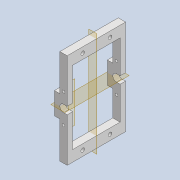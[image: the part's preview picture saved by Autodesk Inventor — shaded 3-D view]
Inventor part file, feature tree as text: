
AUTODESK INVENTOR PART (.ipt)
format: ipt  version: 2020 (Build 240168000, 168)  size: 174,080 bytes
history: native  units: mm
features: reference x8, other x6, extrude x4, sketch x4, plane x3, mirror x2, projected_geometry x2
ambient origin geometry x8: Origin, YZ Plane, XZ Plane, XY Plane, X Axis, Y Axis, Z Axis, Center Point
bodies: Solid1 (feature_tree)
feature tree (29):
  plane  "Work Plane1"
  extrude  "Extrusion1"  Depth=40.0mm
  plane  "Work Plane2"
  extrude  "Extrusion2"  Depth=3.0mm
  extrude  "Extrusion3"  Depth=10.0mm
  mirror  "Mirror1"
  extrude  "Extrusion4"  Depth=4.0mm TaperAngle=0.0deg
  plane  "Work Plane3"
  mirror  "Mirror2"
  sketch  "Sketch2"  dims[d2=26.0mm d3=40.0mm]
  reference  "Reference4"
  reference  "Reference5"
  reference  "Reference6"
  reference  "Reference7"
  sketch  "Sketch3"  dims[d4=6.0mm d5=3.0mm]
  reference  "Reference8"
  projected_geometry  "Projected Loop1"
  sketch  "Sketch4"  dims[d6=4.0mm d7=0.0mm d8=10.0mm]
  reference  "Reference9"
  reference  "Reference10"
  reference  "Reference11"
  sketch  "Sketch5"  dims[d9=12.0mm d10=4.0mm d11=0.0mm d12=4.0mm d13=4.0mm d14=4.0mm d15=0.0mm d16=15.0mm d17=46.0mm d18=2.0mm d19=2.0mm d20=4.0mm d21=0.0mm]
  projected_geometry  "Projected Loop2"
  parser-record x1  (decoder bookkeeping rows leaked as tree rows — omitted from the tree; the rows remain in map.json)
  other  "tip_3_n_base.iam"
  other  "bearing_hh_1:1"
  other  "bearing_hh_1:2"
  other  "pin3_40:1"
  other  "bearing_3_6_2:2"
note: 1 file-system path scrubbed to <path> (originals preserved in map.json)
